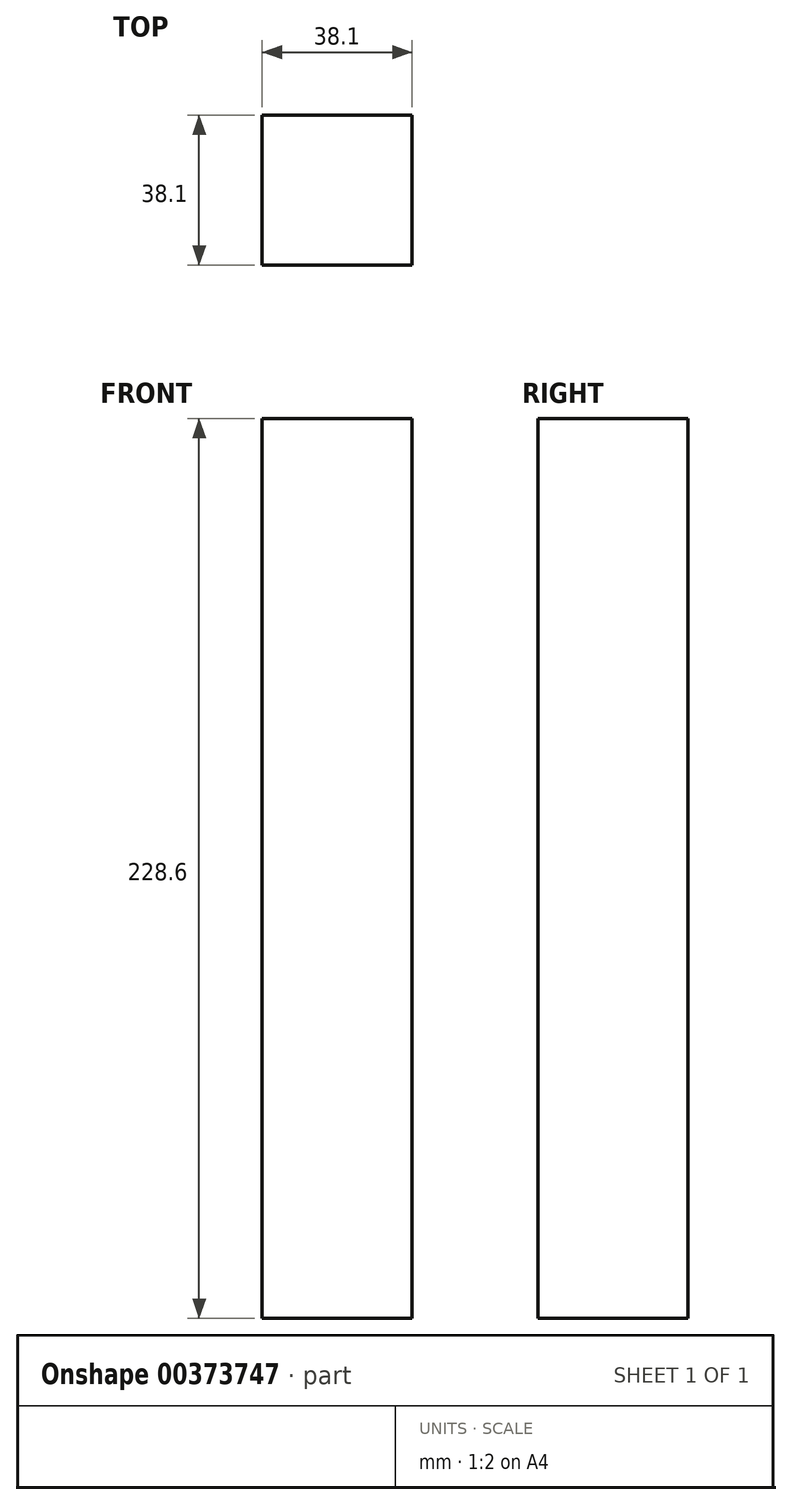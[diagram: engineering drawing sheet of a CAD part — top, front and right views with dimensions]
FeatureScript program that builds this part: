
annotation { "Feature Type Name" : "Feature", "Feature Type Description" : "" }
export const myFeature = defineFeature(function(context is Context, id is Id, definition is map)
    precondition{}
    {
        {
            var Q0;
            Q0=qCreatedBy(makeId("Top.planeOp"),FACE);
            var sketch = newSketch(context, id + "F0", { "sketchPlane" : qUnion([Q0])});
            skLineSegment(sketch, "E0.bottom", {"start": v(-44.83, -38.1) * mm, "end": v(-6.73, -38.1) * mm});
            skLineSegment(sketch, "E0.top", {"start": v(-44.83, 0) * mm, "end": v(-6.73, 0) * mm});
            skLineSegment(sketch, "E0.left", {"start": v(-44.83, -38.1) * mm, "end": v(-44.83, 0) * mm});
            skLineSegment(sketch, "E0.right", {"start": v(-6.73, -38.1) * mm, "end": v(-6.73, 0) * mm});
            skSolve(sketch);
        }
        {
            var Q0;
            Q0=makeQuery(id+"F0.imprint","IMPRINT",FACE,{"disambiguationData":[TD([[makeQuery(id+"F0.imprint","IMPRINT",EDGE,{"derivedFrom":sQuery(id+"F0.wireOp",EDGE,"E0.bottom")}),1.0]])]});
            extrude(context, id + "F1", {"entities" : qUnion([Q0]), "depth" : 228.6 * mm});
        }
    });
